# Revit family: 665_Counter_Overhead_Door
name_source: partatom
category: Doors
units: mm (PartAtom-declared; Revit-internal decimal feet)

## family parameters
Always vertical = Yes
Cut with Voids When Loaded = No
Host = Wall
OmniClass Number = 23.30.10.17.27.11
OmniClass Title = Overhead Coiling
Room Calculation Point = No
Shared = No

## types (4) — shared parameters
Analytic Construction = <None>
Assembly Code = B2030410
Bottom Bar = [Primed Steel Angle with Weatherstrip] [Steel with Locking and Weatherstrip]
Construction Details = https://www.arcat.com
Define Thermal Properties by = Schematic Type
Description = Overhead Door Model 655 Overhead Coiling Steel Counter Door
Door Gap From Wall Interior = 0' - 1 5/16"
Door Track Material = Wood - Red Oak
Elevation From Level = 3' - 2 1/2"
Fire Rating = As Specified in 08 36 00
Function = Interior
Green Building-LEED = https://www.arcat.com
Height = 7' - 2 1/2"
Hood Material = Metal - Steel - Primed
Keynote = 08 33 13
Left End Cap Thickness = 0' - 2 1/2"
Lock Type = [Thumb Turn Locks] [Cylinder Locks]
Manufacturer = Overhead Door Corporation
Maximum Height = 8'  0
Maximum Width = 12'  0
Model = 655
Operator Material = Wood - Red Oak
Panel Height = 4' - 5 1/16"
Panel Width = 9' - 0"
Product Data = http://www.arcat.com
Right End Cap Thickness = 0' - 2 1/2"
Rough Height = 0' - 0"
Rough Width = 9' - 6 1/4"
SpecWizard = https://www.arcat.com
Specification = https://www.arcat.com
Thickness = 0' - 0 1/2"
URL = http://www.overheaddoor.com
Wall Closure = By host
Width = 9' - 0"

## per-type parameters (varying)
| type | Electrical Operator | Has End Caps | Operation | Panel Material |
| Finished Curtain with Primed Steel Hood Manual | No | Yes | [Awning Crank Operator] [Manual - Push Up] | Finishes - Exterior - Gray |
| Finished Curtain with Primed Steel Hood Electric | Yes | No | [Electrical Motor - Push Button Control] [Electrical Motor - Key Operation] [Electrical Motor - Push Button w/ Key] | Finishes - Exterior - Gray |
| Primed Steel Curtain with Primed Steel Hood Manual | No | Yes | [Awning Crank Operator] [Manual - Push Up] | Metal - Steel - Primed |
| Primed Steel Curtain with Primed Steel Hood Electric | Yes | Yes | [Electrical Motor - Push Button Control] [Electrical Motor - Key Operation] [Electrical Motor - Push Button w/ Key] | Metal - Steel - Primed |

## geometry (parser evidence)
native form markers: Sweep x8
no freeform markers — native parametric forms only
